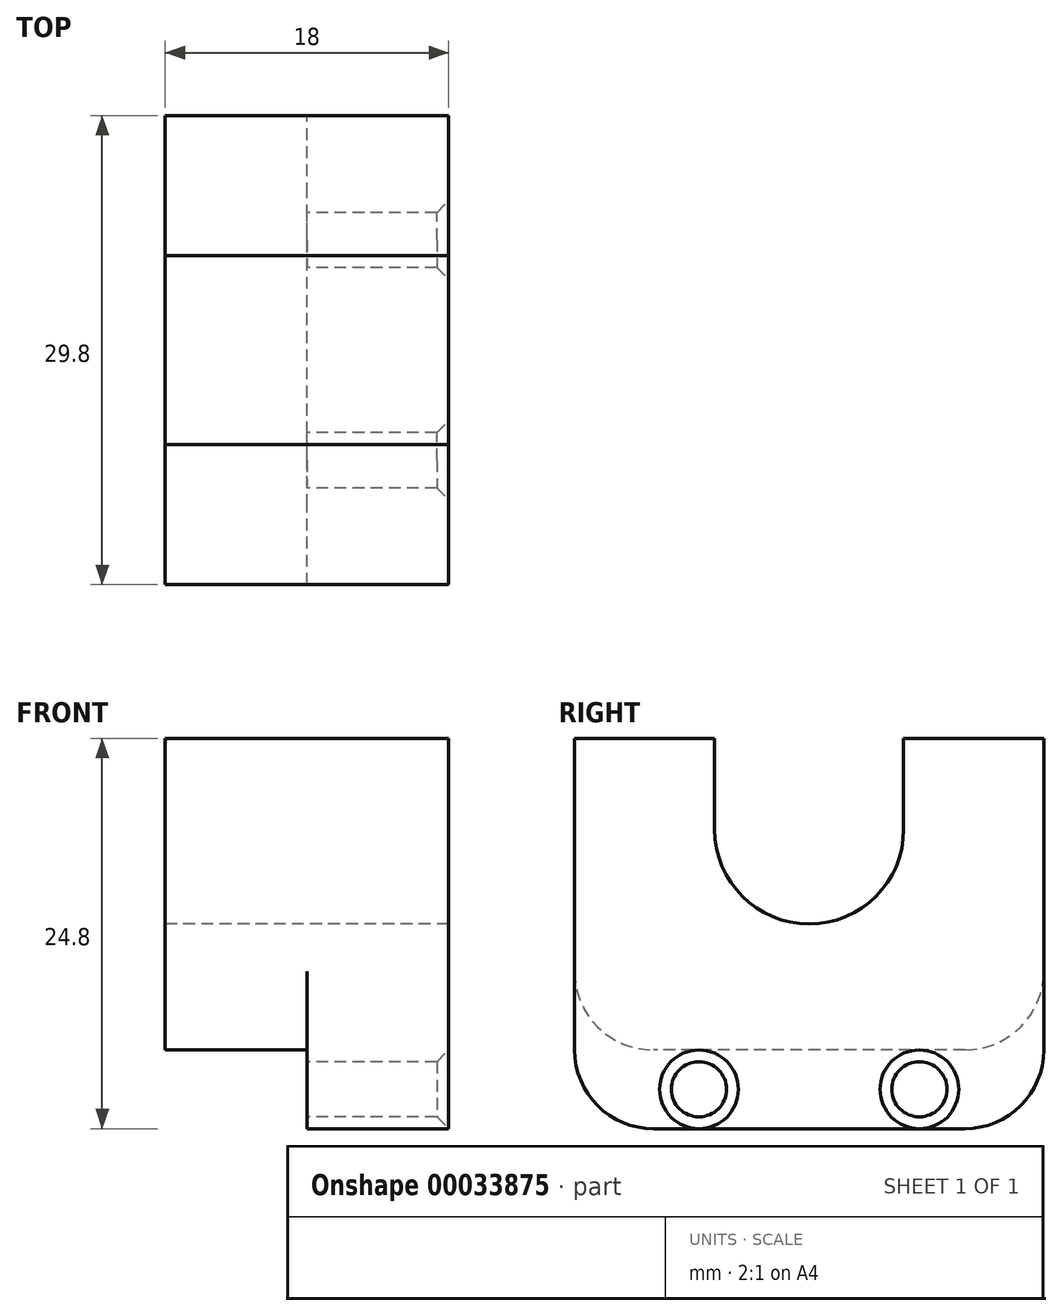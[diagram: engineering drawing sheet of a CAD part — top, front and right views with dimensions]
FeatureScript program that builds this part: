
annotation { "Feature Type Name" : "Feature", "Feature Type Description" : "" }
export const myFeature = defineFeature(function(context is Context, id is Id, definition is map)
    precondition{}
    {
        {
            var Q0;
            Q0=qCreatedBy(makeId("Right.planeOp"),FACE);
            var sketch = newSketch(context, id + "F0", { "sketchPlane" : qUnion([Q0])});
            skLineSegment(sketch, "E0", {"start": v(0, -19.8) * mm, "end": v(0, 0) * mm});
            skLineSegment(sketch, "E1", {"start": v(-29.8, 0) * mm, "end": v(-29.8, -19.8) * mm});
            skPoint(sketch, "E2.visualSharp", {"position": v(0, -24.8) * mm});
            skArc(sketch, "E3.filletArc", {"start": v(-29.8, -19.8) * mm, "mid": v(-28.34, -23.34) * mm, "end": v(-24.8, -24.8) * mm});
            skPoint(sketch, "E4.visualSharp", {"position": v(-29.8, -19.8) * mm});
            skPoint(sketch, "E3.visualSharp", {"position": v(-29.8, -24.8) * mm});
            skPoint(sketch, "E5.visualSharp", {"position": v(0, -19.8) * mm});
            skArc(sketch, "E4.filletArc", {"start": v(-29.8, -14.8) * mm, "mid": v(-28.34, -18.34) * mm, "end": v(-24.8, -19.8) * mm});
            skArc(sketch, "E6", {"start": v(-20.9, -5.8) * mm, "mid": v(-14.9, -11.8) * mm, "end": v(-8.9, -5.8) * mm});
            skArc(sketch, "E5.filletArc", {"start": v(-5, -19.8) * mm, "mid": v(-1.46, -18.34) * mm, "end": v(0, -14.8) * mm});
            skLineSegment(sketch, "E7", {"start": v(-8.9, 0) * mm, "end": v(-8.9, -5.8) * mm});
            skArc(sketch, "E2.filletArc", {"start": v(-5, -24.8) * mm, "mid": v(-1.46, -23.34) * mm, "end": v(0, -19.8) * mm});
            skLineSegment(sketch, "E8", {"start": v(-5, -19.8) * mm, "end": v(-24.8, -19.8) * mm});
            skLineSegment(sketch, "E9", {"start": v(-20.9, -5.8) * mm, "end": v(-20.9, 0) * mm});
            skLineSegment(sketch, "E10", {"start": v(-24.8, -24.8) * mm, "end": v(-5, -24.8) * mm});
            skLineSegment(sketch, "E11", {"start": v(0, 0) * mm, "end": v(-8.9, 0) * mm});
            skLineSegment(sketch, "E12.trimOffspring", {"start": v(-20.9, 0) * mm, "end": v(-29.8, 0) * mm});
            skPoint(sketch, "E13.startSnap0", {"position": v(-14.9, -19.8) * mm});
            skLineSegment(sketch, "E14", {"start": v(-14.9, -27.36) * mm, "end": v(-14.9, -14.87) * mm, "construction": true});
            skSolve(sketch);
        }
        {
            var Q0;
            Q0 = qSketchRegion(id + "F0", true);
            extrude(context, id + "F1", {"entities" : qUnion([Q0]), "depth" : 9 * mm});
        }
        {
            var Q0;
            {var subQ3=sQuery(id+"F0.wireOp",EDGE,"E4.filletArc");Q0=makeQuery(id+"F0.imprint","IMPRINT",FACE,{"disambiguationData":[TD([[makeQuery(id+"F0.imprint","IMPRINT",EDGE,{"derivedFrom":subQ3}),1.0]])]});}
            extrude(context, id + "F2", {"entities" : qUnion([Q0]), "operationType" : NewBodyOperationType.ADD, "oppositeDirection" : true, "depth" : 9 * mm});
        }
        {
            var Q0;
            Q0=makeQuery(id+"F1.opExtrude","CAP_FACE",FACE,{"disambiguationData":[OSD([sQuery(id+"F0.wireOp",EDGE,"E0"),sQuery(id+"F0.wireOp",EDGE,"E1"),sQuery(id+"F0.wireOp",EDGE,"E3.filletArc"),sQuery(id+"F0.wireOp",EDGE,"E6"),sQuery(id+"F0.wireOp",EDGE,"E7"),sQuery(id+"F0.wireOp",EDGE,"E2.filletArc"),sQuery(id+"F0.wireOp",EDGE,"E9"),sQuery(id+"F0.wireOp",EDGE,"E10"),sQuery(id+"F0.wireOp",EDGE,"E11"),sQuery(id+"F0.wireOp",EDGE,"E12.trimOffspring")])],"isStart":false});
            var sketch = newSketch(context, id + "F3", { "sketchPlane" : qUnion([Q0])});
            skPoint(sketch, "E15", {"position": v(-7.9, -22.3) * mm});
            skPoint(sketch, "E16", {"position": v(-21.9, -22.3) * mm});
            skLineSegment(sketch, "E17", {"start": v(-21.9, -22.3) * mm, "end": v(-7.9, -22.3) * mm, "construction": true});
            skPoint(sketch, "E18", {"position": v(-14.9, -22.3) * mm});
            skSolve(sketch);
        }
        {
            var Q0;
            Q0=sQuery(id+"F3.wireOp",VERTEX,"E16");
            var Q1;
            Q1=sQuery(id+"F3.wireOp",VERTEX,"E15");
            var Q2;
            Q2=makeQuery(id+"F1.opExtrude","SWEPT_BODY",BODY,{"disambiguationData":[OSD([sQuery(id+"F0.wireOp",EDGE,"E0"),sQuery(id+"F0.wireOp",EDGE,"E1"),sQuery(id+"F0.wireOp",EDGE,"E3.filletArc"),sQuery(id+"F0.wireOp",EDGE,"E6"),sQuery(id+"F0.wireOp",EDGE,"E7"),sQuery(id+"F0.wireOp",EDGE,"E2.filletArc"),sQuery(id+"F0.wireOp",EDGE,"E9"),sQuery(id+"F0.wireOp",EDGE,"E10"),sQuery(id+"F0.wireOp",EDGE,"E11"),sQuery(id+"F0.wireOp",EDGE,"E12.trimOffspring")])]});
            hole(context, id + "F4", {"style" : HoleStyle.C_SINK, "holeDiameter" : 3.5 * mm, "cSinkDiameter" : 5 * mm, "endStyle" : HoleEndStyle.THROUGH, "locations" : qUnion([Q0, Q1]), "scope" : qUnion([Q2]), "cSinkAngle" : 90 * degree});
        }
    });
